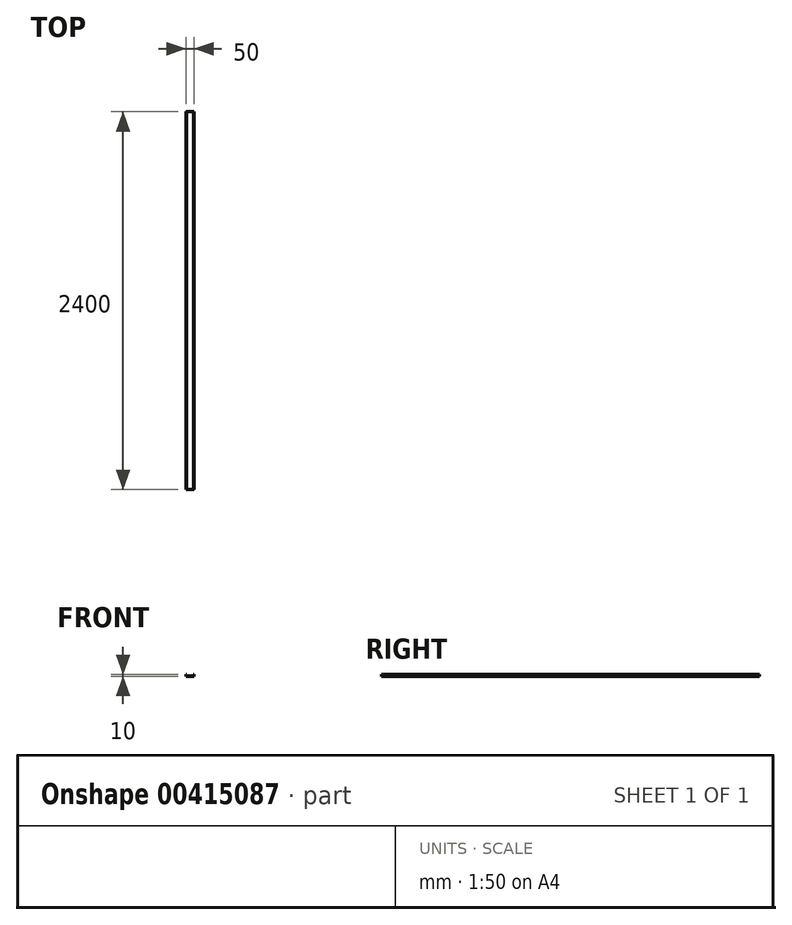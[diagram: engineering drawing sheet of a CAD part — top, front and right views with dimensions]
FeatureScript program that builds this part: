
annotation { "Feature Type Name" : "Feature", "Feature Type Description" : "" }
export const myFeature = defineFeature(function(context is Context, id is Id, definition is map)
    precondition{}
    {
        {
            var Q0;
            Q0=qCreatedBy(makeId("Front.planeOp"),FACE);
            var sketch = newSketch(context, id + "F0", { "sketchPlane" : qUnion([Q0])});
            skLineSegment(sketch, "E0", {"start": v(0, 0) * mm, "end": v(50, 0) * mm});
            skLineSegment(sketch, "E1", {"start": v(50, 0) * mm, "end": v(50, 10) * mm});
            skLineSegment(sketch, "E2", {"start": v(0, 0) * mm, "end": v(0, 10) * mm});
            skLineSegment(sketch, "E3.0", {"start": v(3, 5) * mm, "end": v(3, 10) * mm});
            skLineSegment(sketch, "E3.1", {"start": v(5, 3) * mm, "end": v(45, 3) * mm});
            skLineSegment(sketch, "E3.2", {"start": v(47, 5) * mm, "end": v(47, 10) * mm});
            skLineSegment(sketch, "E4", {"start": v(0, 10) * mm, "end": v(3, 10) * mm});
            skLineSegment(sketch, "E5", {"start": v(47, 10) * mm, "end": v(50, 10) * mm});
            skPoint(sketch, "E6.visualSharp", {"position": v(3, 3) * mm});
            skArc(sketch, "E6.filletArc", {"start": v(3, 5) * mm, "mid": v(3.59, 3.59) * mm, "end": v(5, 3) * mm});
            skPoint(sketch, "E7.visualSharp", {"position": v(47, 3) * mm});
            skArc(sketch, "E7.filletArc", {"start": v(45, 3) * mm, "mid": v(46.41, 3.59) * mm, "end": v(47, 5) * mm});
            skSolve(sketch);
        }
        {
            var Q0;
            Q0 = qSketchRegion(id + "F0", true);
            extrude(context, id + "F1", {"entities" : qUnion([Q0]), "oppositeDirection" : true, "depth" : 2400 * mm});
        }
    });
